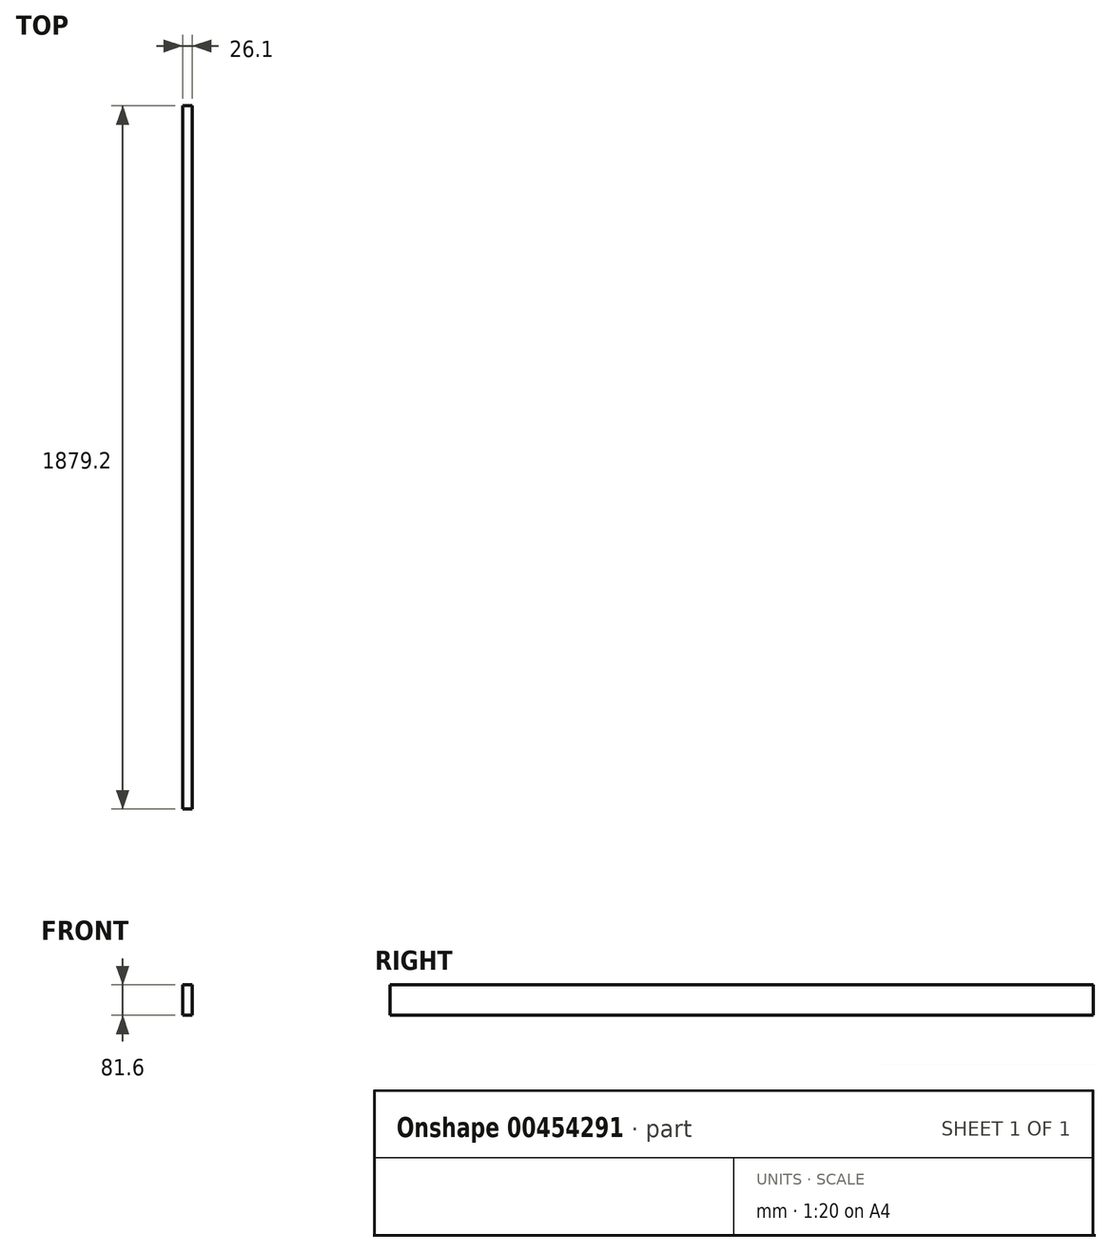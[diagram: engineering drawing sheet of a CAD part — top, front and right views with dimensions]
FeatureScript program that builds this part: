
annotation { "Feature Type Name" : "Feature", "Feature Type Description" : "" }
export const myFeature = defineFeature(function(context is Context, id is Id, definition is map)
    precondition{}
    {
        {
            var Q0;
            Q0=qCreatedBy(makeId("Right.planeOp"),FACE);
            var sketch = newSketch(context, id + "F0", { "sketchPlane" : qUnion([Q0])});
            skLineSegment(sketch, "E0.bottom", {"start": v(939.6, -40.8) * mm, "end": v(-939.6, -40.8) * mm});
            skLineSegment(sketch, "E0.top", {"start": v(939.6, 40.8) * mm, "end": v(-939.6, 40.8) * mm});
            skLineSegment(sketch, "E0.left", {"start": v(939.6, -40.8) * mm, "end": v(939.6, 40.8) * mm});
            skLineSegment(sketch, "E0.right", {"start": v(-939.6, -40.8) * mm, "end": v(-939.6, 40.8) * mm});
            skPoint(sketch, "E0.middle", {"position": v(0, 0) * mm});
            skSolve(sketch);
        }
        {
            var Q0;
            Q0=makeQuery(id+"F0.imprint","IMPRINT",FACE,{"disambiguationData":[TD([[makeQuery(id+"F0.imprint","IMPRINT",EDGE,{"derivedFrom":sQuery(id+"F0.wireOp",EDGE,"E0.bottom")}),-1.0]])]});
            extrude(context, id + "F1", {"entities" : qUnion([Q0]), "depth" : 26.1 * mm});
        }
    });
